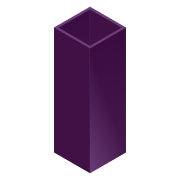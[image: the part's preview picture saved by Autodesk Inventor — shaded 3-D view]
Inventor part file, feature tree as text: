
AUTODESK INVENTOR PART (.ipt)
format: ipt  version: 2012 (Build 160160000, 160)  size: 76,800 bytes
history: native  units: in
note: dims shown in document units (in); Inventor stores cm internally (conversion verified against a paired STEP export)
features: extrude x1, shell x1, sketch x1
ambient origin geometry x8: Origin, YZ Plane, XZ Plane, XY Plane, X Axis, Y Axis, Z Axis, Center Point
bodies: Solid1 (feature_tree)
feature tree (3):
  extrude  "Extrusion1"  Depth=3.0in
  shell  "Shell1"  Thickness=1.0in
  sketch  "Sketch1"  dims[d0=1.0in d1=3.0in d2=1.0in d3=0.0in d4=0.0625in]
